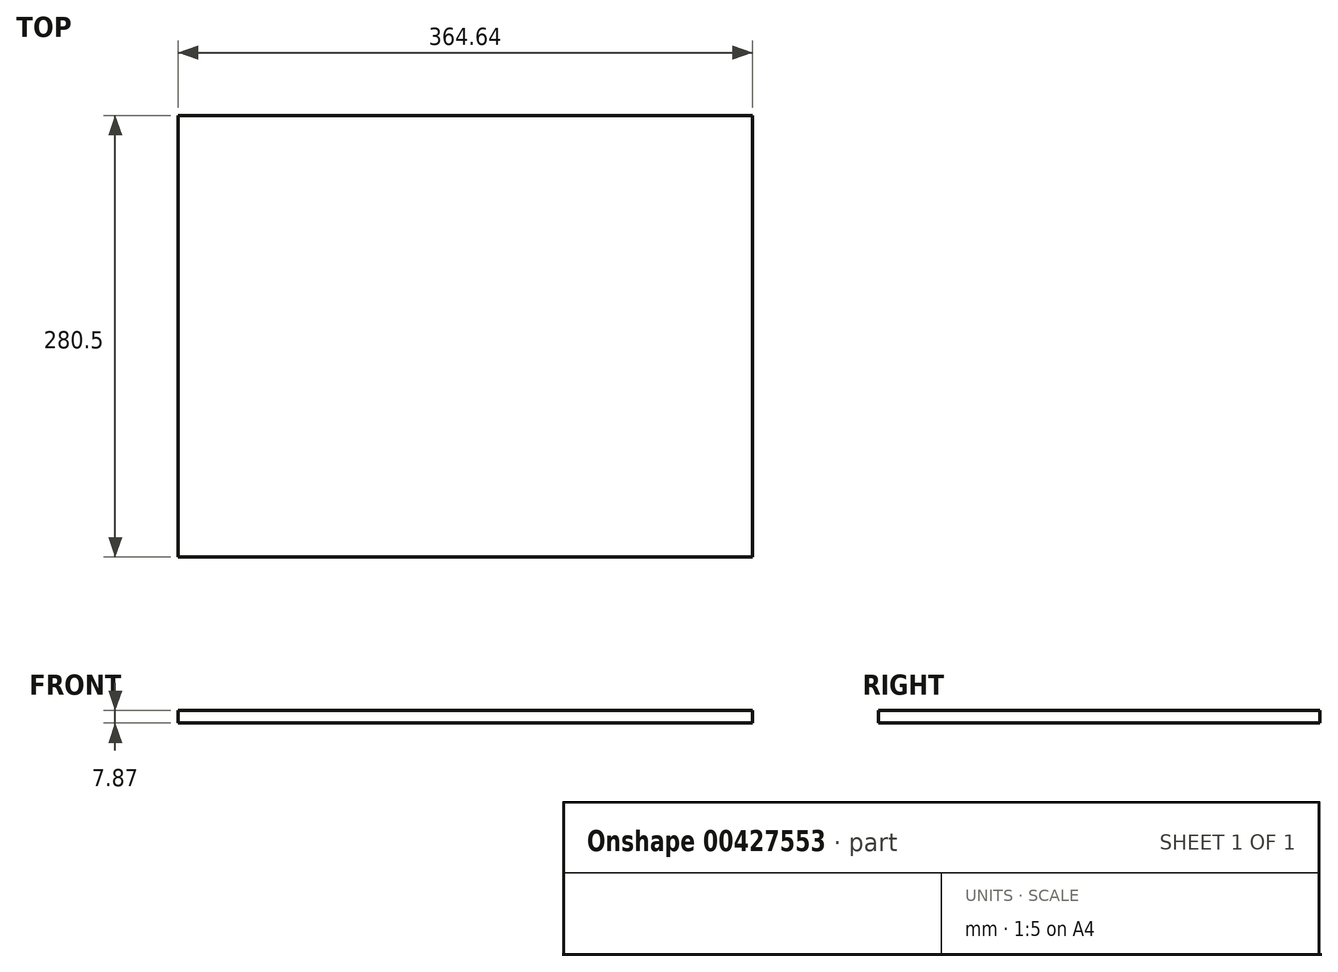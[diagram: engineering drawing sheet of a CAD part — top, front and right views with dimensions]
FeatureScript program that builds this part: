
annotation { "Feature Type Name" : "Feature", "Feature Type Description" : "" }
export const myFeature = defineFeature(function(context is Context, id is Id, definition is map)
    precondition{}
    {
        {
            var Q0;
            Q0=qCreatedBy(makeId("Top.planeOp"),FACE);
            var sketch = newSketch(context, id + "F0", { "sketchPlane" : qUnion([Q0])});
            skLineSegment(sketch, "E0.bottom", {"start": v(-182.32, 140.25) * mm, "end": v(182.32, 140.25) * mm});
            skLineSegment(sketch, "E0.top", {"start": v(-182.32, -140.25) * mm, "end": v(182.32, -140.25) * mm});
            skLineSegment(sketch, "E0.left", {"start": v(-182.32, 140.25) * mm, "end": v(-182.32, -140.25) * mm});
            skLineSegment(sketch, "E0.right", {"start": v(182.32, 140.25) * mm, "end": v(182.32, -140.25) * mm});
            skPoint(sketch, "E0.middle", {"position": v(0, 0) * mm});
            skSolve(sketch);
        }
        {
            var Q0;
            Q0 = qSketchRegion(id + "F0", true);
            extrude(context, id + "F1", {"entities" : qUnion([Q0]), "depth" : 7.87 * mm});
        }
    });
